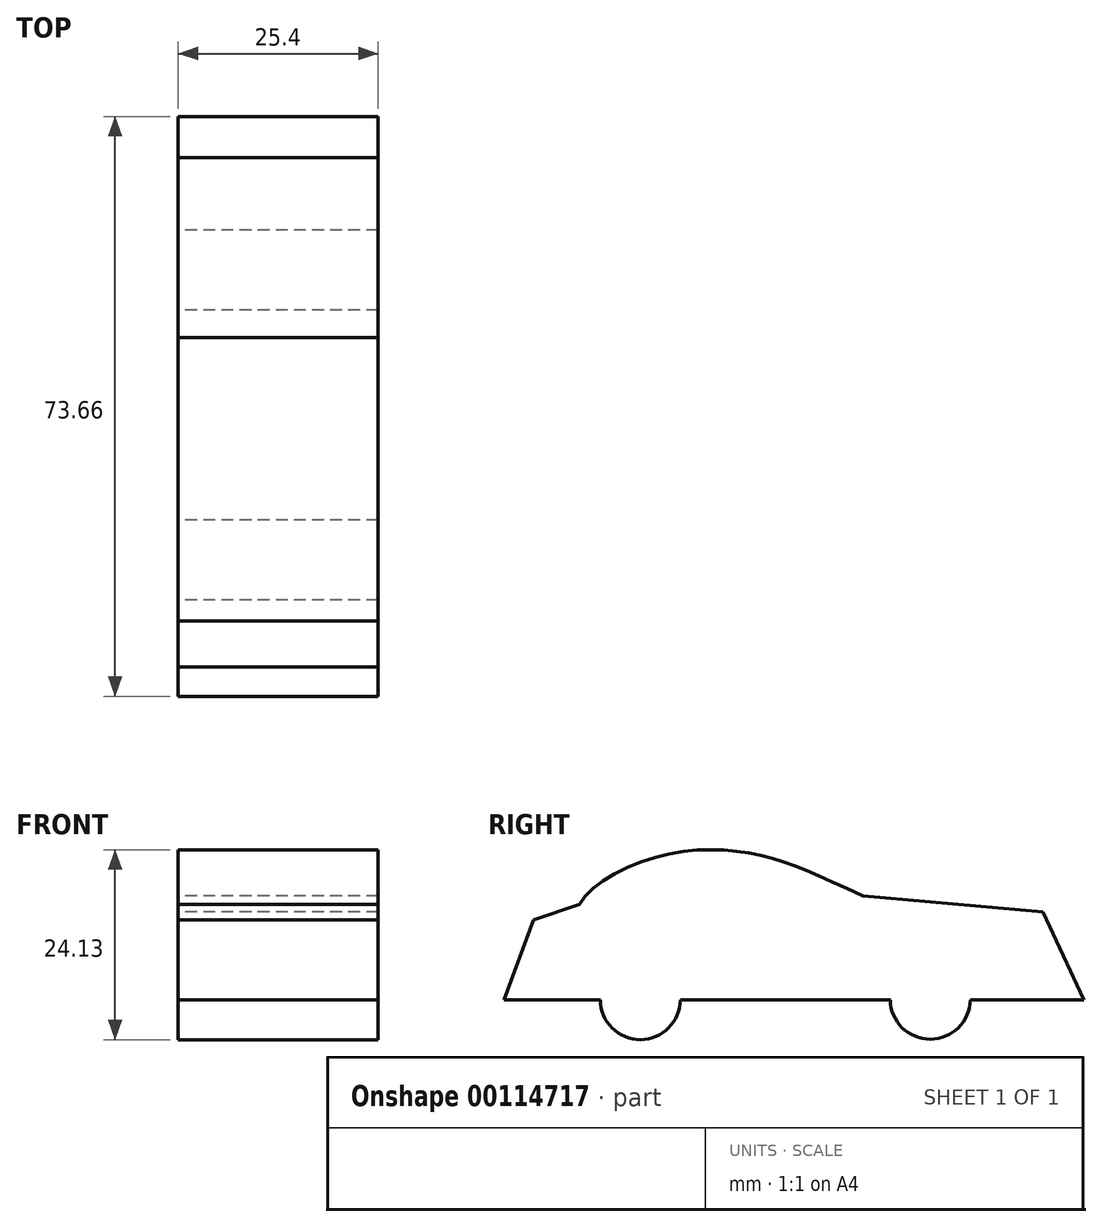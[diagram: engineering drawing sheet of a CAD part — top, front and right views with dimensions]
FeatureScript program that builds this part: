
annotation { "Feature Type Name" : "Feature", "Feature Type Description" : "" }
export const myFeature = defineFeature(function(context is Context, id is Id, definition is map)
    precondition{}
    {
        {
            var Q0;
            Q0=qCreatedBy(makeId("Right.planeOp"),FACE);
            var sketch = newSketch(context, id + "F0", { "sketchPlane" : qUnion([Q0])});
            skLineSegment(sketch, "E0", {"start": v(13.97, 0) * mm, "end": v(-12.7, 0) * mm});
            skLineSegment(sketch, "E1", {"start": v(-22.86, 0) * mm, "end": v(-35.08, 0) * mm});
            skLineSegment(sketch, "E2", {"start": v(-35.08, 0) * mm, "end": v(-31.36, 10.16) * mm});
            skLineSegment(sketch, "E3", {"start": v(-31.36, 10.16) * mm, "end": v(-25.52, 12.12) * mm});
            skLineSegment(sketch, "E4", {"start": v(24.13, 0) * mm, "end": v(38.58, 0) * mm});
            skLineSegment(sketch, "E5", {"start": v(38.58, 0) * mm, "end": v(33.36, 11.18) * mm});
            skLineSegment(sketch, "E6", {"start": v(33.36, 11.18) * mm, "end": v(10.5, 13.18) * mm});
            skArc(sketch, "E7", {"start": v(-22.86, 0) * mm, "mid": v(-17.78, -5.08) * mm, "end": v(-12.7, 0) * mm});
            skArc(sketch, "E8", {"start": v(13.97, 0) * mm, "mid": v(19.05, -5.02) * mm, "end": v(24.13, 0) * mm});
            skFitSpline(sketch, "E9", {"points": [v(10.5, 13.18) * mm, v(-2.4, 18.3) * mm, v(-15.1, 18.29) * mm, v(-25.52, 12.12) * mm], "startDerivative": vector(-49.89, 22.88) * mm, "endDerivative": vector(-12.45, -24.05) * mm});
            skSolve(sketch);
        }
        {
            var Q0;
            Q0=makeQuery(id+"F0.imprint","IMPRINT",FACE,{"disambiguationData":[TD([[makeQuery(id+"F0.imprint","IMPRINT",EDGE,{"derivedFrom":sQuery(id+"F0.wireOp",EDGE,"E0")}),-1.0]])]});
            extrude(context, id + "F1", {"entities" : qUnion([Q0]), "endBound" : BoundingType.SYMMETRIC, "depth" : 25.4 * mm});
        }
    });
